# Revit family: ITK 19 вентиляционный модуль 1U 4 вентилятора с цифровым термостатом
name_source: partatom
category: Электрооборудование
revit_build: Autodesk Revit 2016 (Build: 20160314_0715(x64)
units: mm (PartAtom-declared; Revit-internal decimal feet)

## family parameters
Всегда вертикально = Да
На основе рабочей плоскости = Нет
Общий = Нет
При загрузке вырезать с полостями = Нет
Размер круглого соединителя = Использовать диаметр
Тип детали = Другая панель
Точка расчета площади = Нет

## types (1)
- FM05-1U4TS
    ADSK_Единица измерения = шт
    ADSK_Завод-изготовитель = IEK
    ADSK_Классификация нагрузок = Прочее
    ADSK_Количество фаз = 1
    ADSK_Количество фаз числовое = 1
    ADSK_Коэффициент мощности = 1
    ADSK_Марка = FM05-1U4TS
    ADSK_Масса = 0
    ADSK_Наименование = ITK 19" вентил. модуль 1U 4 вентилятора с цифровым термостатом
    ADSK_Наименование краткое = FM05-1U4TS
    ADSK_Напряжение = 220 В
    ADSK_Номинальная мощность = 0 Вт
    ADSK_Полная мощность = 0 В·А
    ADSK_Ток = 0 А
    URL = http://www.itk-group.ru
    Высота = 44 мм
    Глубина = 542 мм
    Изготовитель = ITK
    Материал = Окраска - RAL 9005
    Описание = 19-дюймовые вентиляторные модули предназначены для установки и использования в любых шкафах ITK и служат для организации принудительного охлаждения и вентиляции установленного в них активного оборудования.

Вентиляторные модули имеют два или четыре вентилятора, заключенных в единый металлический корпус черного цвета высотой 1U, комплектуются выключателем со светоиндикацией и цифровым термостатом с дисплеем. Диапазон регулировки температуры термостата: от 0 до 60°С. Номинальное рабочее напряжение: 230В. Частота тока: 50Гц. Минимальный срок службы: 50 тыс. часов. Подача рабочего напряжения на вентиляторный модуль осуществляется через встроенный кабель электропитания длиной 2 метра и вилкой немецкого стандарта (евровилка).

Модули устанавливаются на 19-дюймовые монтажные профили над оборудованием, требующим локального охлаждения в конкретном месте шкафа, занимая при этом 1U высоты шкафа.
Совместимы со всеми 19-доймовыми шкафами и стойками ITK.
Обладают современным привлекательным дизайном и продуманной конструкцией.
Удобны в монтаже и эксплуатации.
Соответствие международным стандартам ISO9001, IEC 297, ISO/IEC 11801. 
Сертифицированы по ГОСТ Р.
Все аксессуары идут с крепежом.
Возможно исполнение в двух цветах: серый (RAL7035) и черный (RAL9005).
Всегда в наличии на складе.
Гарантия на все аксессуары до 2-х лет.
    Ширина = 483 мм
